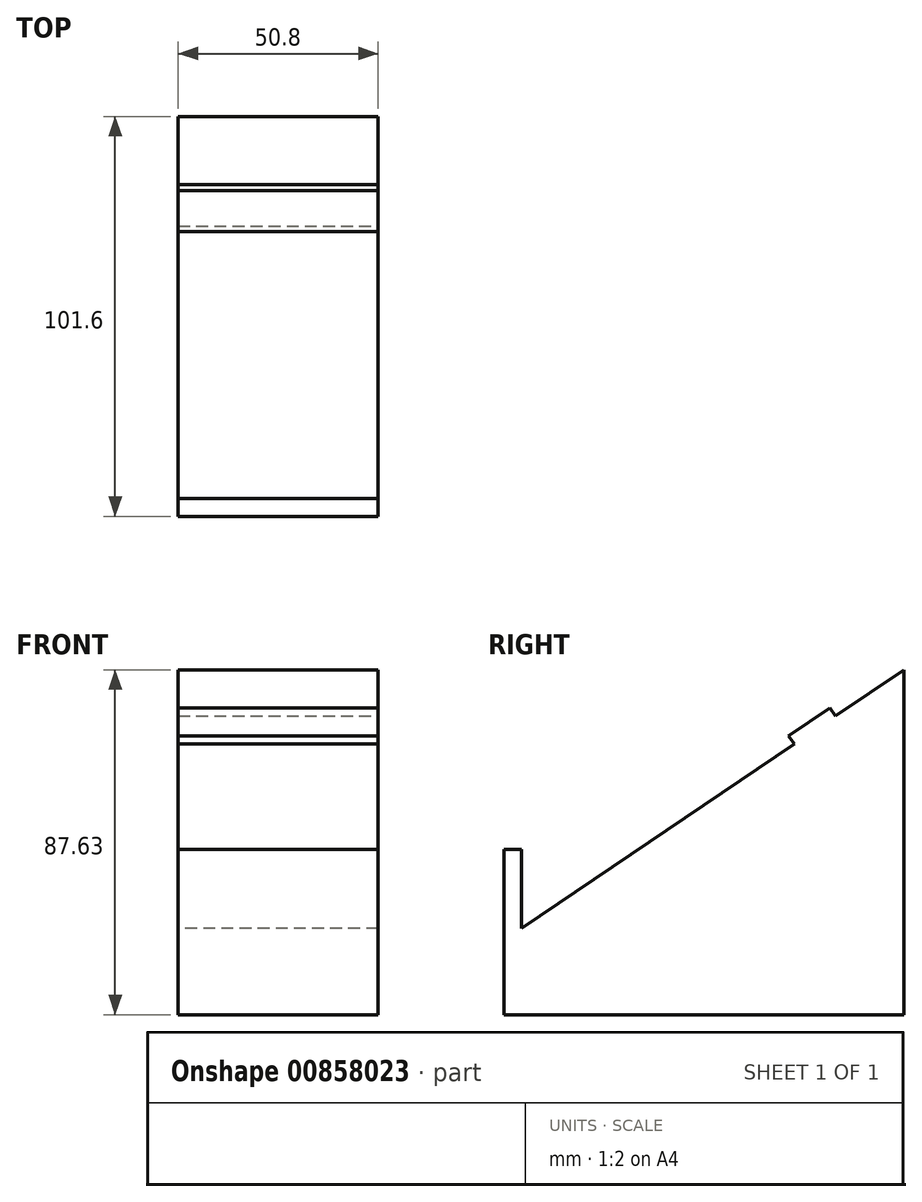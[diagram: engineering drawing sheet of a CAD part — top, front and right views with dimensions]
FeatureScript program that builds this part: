
annotation { "Feature Type Name" : "Feature", "Feature Type Description" : "" }
export const myFeature = defineFeature(function(context is Context, id is Id, definition is map)
    precondition{}
    {
        {
            var Q0;
            Q0=qCreatedBy(makeId("Right.planeOp"),FACE);
            var sketch = newSketch(context, id + "F0", { "sketchPlane" : qUnion([Q0])});
            skLineSegment(sketch, "E0", {"start": v(-101.6, 18.93) * mm, "end": v(-101.6, 0) * mm});
            skLineSegment(sketch, "E1", {"start": v(-101.6, 18.93) * mm, "end": v(0, 87.63) * mm});
            skLineSegment(sketch, "E2", {"start": v(0, 87.63) * mm, "end": v(0, 0) * mm});
            skLineSegment(sketch, "E3", {"start": v(-101.6, 0) * mm, "end": v(0, 0) * mm});
            skLineSegment(sketch, "E4", {"start": v(-101.6, 18.93) * mm, "end": v(-101.6, 42.04) * mm});
            skLineSegment(sketch, "E5", {"start": v(-101.6, 42.04) * mm, "end": v(-97.12, 42.04) * mm});
            skLineSegment(sketch, "E6", {"start": v(-97.12, 42.04) * mm, "end": v(-97.12, 21.96) * mm});
            skSolve(sketch);
        }
        {
            var Q0;
            {var subQ3=sQuery(id+"F0.wireOp",EDGE,"E0");Q0=makeQuery(id+"F0.imprint","IMPRINT",FACE,{"disambiguationData":[TD([[makeQuery(id+"F0.imprint","IMPRINT",EDGE,{"derivedFrom":subQ3}),1.0]])]});}
            var Q1;
            {var subQ0=sQuery(id+"F0.wireOp",EDGE,"E4");Q1=makeQuery(id+"F0.imprint","IMPRINT",FACE,{"disambiguationData":[TD([[makeQuery(id+"F0.imprint","IMPRINT",EDGE,{"derivedFrom":subQ0}),-1.0]])]});}
            extrude(context, id + "F1", {"entities" : qUnion([Q0, Q1]), "depth" : 50.8 * mm, "offsetDistance" : 25.4 * mm});
        }
        {
            var Q0;
            Q0=makeQuery(id+"F1.opExtrude","SWEPT_FACE",FACE,{"disambiguationData":[OSD([sQuery(id+"F0.wireOp",EDGE,"E1")])]});
            var sketch = newSketch(context, id + "F2", { "sketchPlane" : qUnion([Q0])});
            skLineSegment(sketch, "E7.bottom", {"start": v(0, 28.12) * mm, "end": v(50.8, 28.12) * mm});
            skLineSegment(sketch, "E7.top", {"start": v(0, 15.42) * mm, "end": v(50.8, 15.42) * mm});
            skLineSegment(sketch, "E7.left", {"start": v(0, 28.12) * mm, "end": v(0, 15.42) * mm});
            skLineSegment(sketch, "E7.right", {"start": v(50.8, 28.12) * mm, "end": v(50.8, 15.42) * mm});
            skLineSegment(sketch, "E8.bottom", {"start": v(0, 1.17) * mm, "end": v(50.8, 1.17) * mm});
            skLineSegment(sketch, "E8.top", {"start": v(0, -11.53) * mm, "end": v(50.8, -11.53) * mm});
            skLineSegment(sketch, "E8.left", {"start": v(0, 1.17) * mm, "end": v(0, -11.53) * mm});
            skLineSegment(sketch, "E8.right", {"start": v(50.8, 1.17) * mm, "end": v(50.8, -11.53) * mm});
            skSolve(sketch);
        }
        {
            var Q0;
            Q0=makeQuery(id+"F2.imprint","IMPRINT",FACE,{"disambiguationData":[TD([[makeQuery(id+"F2.imprint","IMPRINT",EDGE,{"derivedFrom":sQuery(id+"F2.wireOp",EDGE,"E7.bottom")}),-1.0]])]});
            extrude(context, id + "F3", {"entities" : qUnion([Q0]), "operationType" : NewBodyOperationType.ADD, "depth" : 2.54 * mm, "offsetDistance" : 25.4 * mm});
        }
    });
